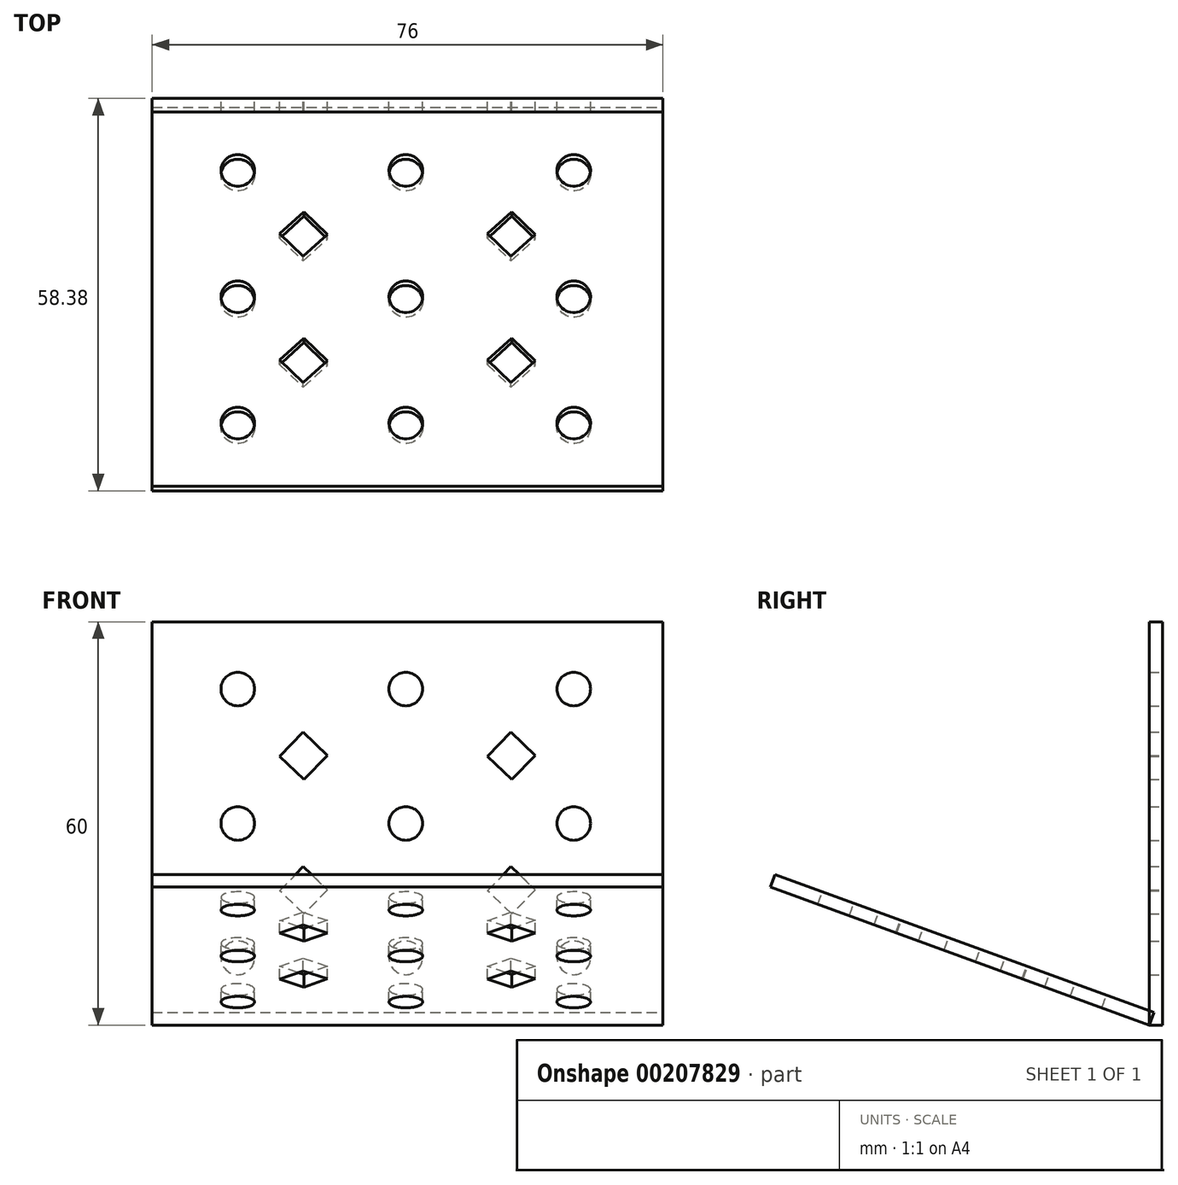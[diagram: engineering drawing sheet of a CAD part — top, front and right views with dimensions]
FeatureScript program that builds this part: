
annotation { "Feature Type Name" : "Feature", "Feature Type Description" : "" }
export const myFeature = defineFeature(function(context is Context, id is Id, definition is map)
    precondition{}
    {
        {
            assignVariable(context, id + "F0", {"name" : "PlateThickness", "anyValue" : 2 * mm});
        }
        {
            var Q0;
            Q0=qCreatedBy(makeId("Front.planeOp"),FACE);
            var sketch = newSketch(context, id + "F1", { "sketchPlane" : qUnion([Q0])});
            skLineSegment(sketch, "E0.bottom", {"start": v(-38, 0) * mm, "end": v(38, 0) * mm});
            skLineSegment(sketch, "E0.top", {"start": v(-38, 60) * mm, "end": v(38, 60) * mm});
            skLineSegment(sketch, "E0.left", {"start": v(-38, 0) * mm, "end": v(-38, 60) * mm});
            skLineSegment(sketch, "E0.right", {"start": v(38, 0) * mm, "end": v(38, 60) * mm});
            skCircle(sketch, "E1", {"center": v(-25.25, 50) * mm, "radius": 2.5 * mm});
            skLineSegment(sketch, "E2", {"start": v(-19, 40) * mm, "end": v(-15.53, 43.6) * mm});
            skLineSegment(sketch, "E3", {"start": v(-15.53, 43.6) * mm, "end": v(-11.93, 40.12) * mm});
            skLineSegment(sketch, "E4", {"start": v(-11.93, 40.12) * mm, "end": v(-15.4, 36.53) * mm});
            skLineSegment(sketch, "E5", {"start": v(-15.4, 36.53) * mm, "end": v(-19, 40) * mm});
            skCircle(sketch, "E6.0.1.0", {"center": v(-25.25, 30) * mm, "radius": 2.5 * mm});
            skCircle(sketch, "E6.0.2.0", {"center": v(-25.25, 10) * mm, "radius": 2.5 * mm});
            skCircle(sketch, "E6.1.0.0", {"center": v(-0.25, 50) * mm, "radius": 2.5 * mm});
            skCircle(sketch, "E6.1.1.0", {"center": v(-0.25, 30) * mm, "radius": 2.5 * mm});
            skCircle(sketch, "E6.1.2.0", {"center": v(-0.25, 10) * mm, "radius": 2.5 * mm});
            skLineSegment(sketch, "E6.direction1", {"start": v(-25.25, 50) * mm, "end": v(-0.25, 50) * mm, "construction": true});
            skLineSegment(sketch, "E6.direction2", {"start": v(-25.25, 50) * mm, "end": v(-25.25, 30) * mm, "construction": true});
            skCircle(sketch, "E7.0.2.0", {"center": v(24.75, 50) * mm, "radius": 2.5 * mm});
            skCircle(sketch, "E7.0.2.1", {"center": v(24.75, 30) * mm, "radius": 2.5 * mm});
            skCircle(sketch, "E7.0.2.2", {"center": v(24.75, 10) * mm, "radius": 2.5 * mm});
            skLineSegment(sketch, "E8.0.1.0", {"start": v(-11.93, 20.12) * mm, "end": v(-15.4, 16.53) * mm});
            skLineSegment(sketch, "E8.0.1.1", {"start": v(-15.4, 16.53) * mm, "end": v(-19, 20) * mm});
            skLineSegment(sketch, "E8.0.1.2", {"start": v(-15.53, 23.6) * mm, "end": v(-11.93, 20.12) * mm});
            skLineSegment(sketch, "E8.0.1.3", {"start": v(-19, 20) * mm, "end": v(-15.53, 23.6) * mm});
            skLineSegment(sketch, "E8.1.0.0", {"start": v(19, 40.12) * mm, "end": v(15.53, 36.53) * mm});
            skLineSegment(sketch, "E8.1.0.1", {"start": v(15.53, 36.53) * mm, "end": v(11.93, 40) * mm});
            skLineSegment(sketch, "E8.1.0.2", {"start": v(15.4, 43.6) * mm, "end": v(19, 40.12) * mm});
            skLineSegment(sketch, "E8.1.0.3", {"start": v(11.93, 40) * mm, "end": v(15.4, 43.6) * mm});
            skLineSegment(sketch, "E8.1.1.0", {"start": v(19, 20.12) * mm, "end": v(15.53, 16.53) * mm});
            skLineSegment(sketch, "E8.1.1.1", {"start": v(15.53, 16.53) * mm, "end": v(11.93, 20) * mm});
            skLineSegment(sketch, "E8.1.1.2", {"start": v(15.4, 23.6) * mm, "end": v(19, 20.12) * mm});
            skLineSegment(sketch, "E8.1.1.3", {"start": v(11.93, 20) * mm, "end": v(15.4, 23.6) * mm});
            skLineSegment(sketch, "E8.direction1", {"start": v(-19, 40) * mm, "end": v(11.93, 40) * mm, "construction": true});
            skLineSegment(sketch, "E8.direction2", {"start": v(-19, 40) * mm, "end": v(-19, 20) * mm, "construction": true});
            skSolve(sketch);
        }
        {
            var Q0;
            Q0=qSketchRegion(id+"F1",true);
            extrude(context, id + "F2", {"entities" : qUnion([Q0]), "depth" : getVariable(context, 'PlateThickness')});
        }
        {
            var Q0;
            Q0=makeQuery(id+"F2.opExtrude","SWEPT_BODY",BODY,{"disambiguationData":[OSD([sQuery(id+"F1.wireOp",EDGE,"E0.bottom"),sQuery(id+"F1.wireOp",EDGE,"E0.top"),sQuery(id+"F1.wireOp",EDGE,"E0.left"),sQuery(id+"F1.wireOp",EDGE,"E0.right"),sQuery(id+"F1.wireOp",EDGE,"E1"),sQuery(id+"F1.wireOp",EDGE,"E2"),sQuery(id+"F1.wireOp",EDGE,"E3"),sQuery(id+"F1.wireOp",EDGE,"E4"),sQuery(id+"F1.wireOp",EDGE,"E5"),sQuery(id+"F1.wireOp",EDGE,"E6.0.1.0"),sQuery(id+"F1.wireOp",EDGE,"E6.0.2.0"),sQuery(id+"F1.wireOp",EDGE,"E6.1.0.0"),sQuery(id+"F1.wireOp",EDGE,"E6.1.1.0"),sQuery(id+"F1.wireOp",EDGE,"E6.1.2.0"),sQuery(id+"F1.wireOp",EDGE,"E7.0.2.0"),sQuery(id+"F1.wireOp",EDGE,"E7.0.2.1"),sQuery(id+"F1.wireOp",EDGE,"E7.0.2.2"),sQuery(id+"F1.wireOp",EDGE,"E8.0.1.0"),sQuery(id+"F1.wireOp",EDGE,"E8.0.1.1"),sQuery(id+"F1.wireOp",EDGE,"E8.0.1.2"),sQuery(id+"F1.wireOp",EDGE,"E8.0.1.3"),sQuery(id+"F1.wireOp",EDGE,"E8.1.0.0"),sQuery(id+"F1.wireOp",EDGE,"E8.1.0.1"),sQuery(id+"F1.wireOp",EDGE,"E8.1.0.2"),sQuery(id+"F1.wireOp",EDGE,"E8.1.0.3"),sQuery(id+"F1.wireOp",EDGE,"E8.1.1.0"),sQuery(id+"F1.wireOp",EDGE,"E8.1.1.1"),sQuery(id+"F1.wireOp",EDGE,"E8.1.1.2"),sQuery(id+"F1.wireOp",EDGE,"E8.1.1.3")])]});
            var Q1;
            Q1=makeQuery(id+"F2.opExtrude","CAP_EDGE",EDGE,{"disambiguationData":[OSD([sQuery(id+"F1.wireOp",EDGE,"E0.bottom")])],"isStart":false});
            transform(context, id + "F3", {"entities" : qUnion([Q0]), "transformType" : TransformType.ROTATION, "transformAxis" : qUnion([Q1]), "angle" : 70 * degree, "makeCopy" : true});
        }
    });
